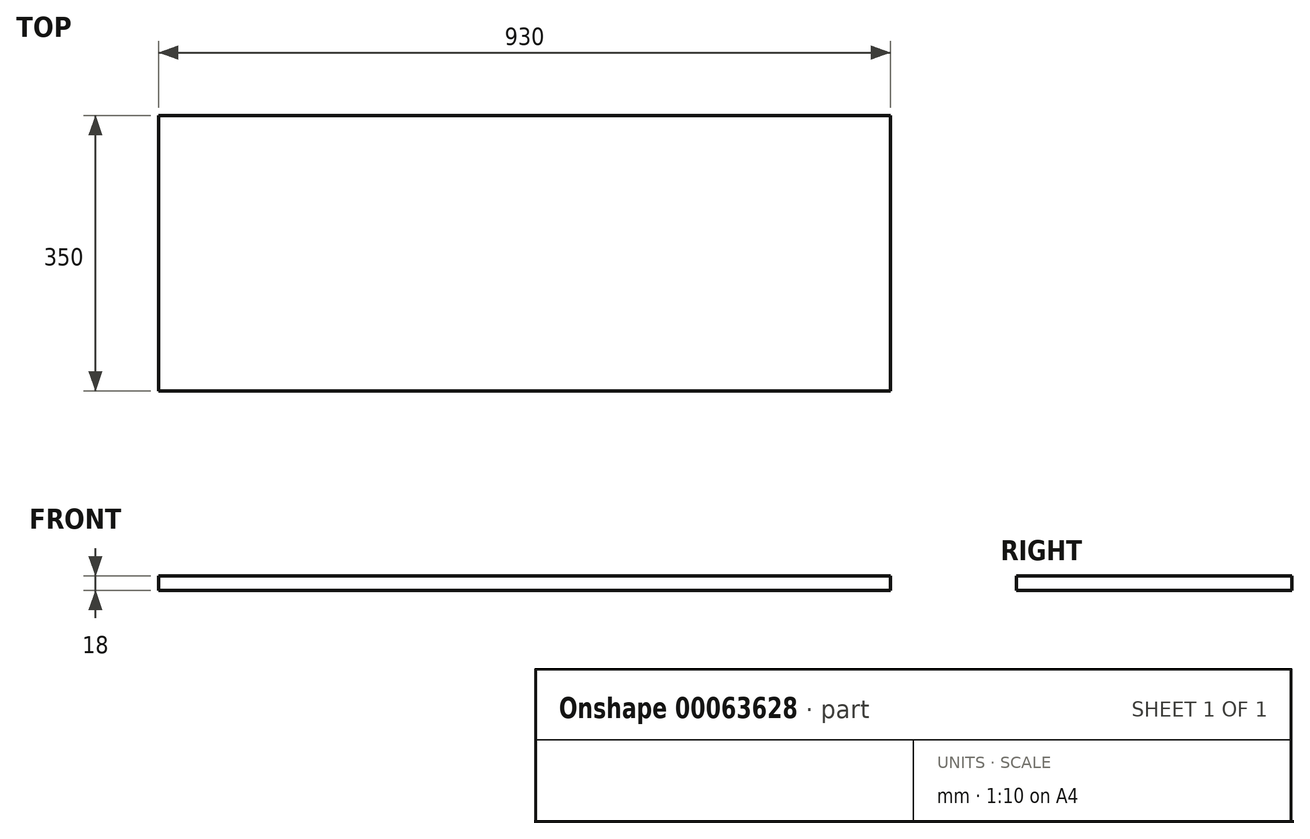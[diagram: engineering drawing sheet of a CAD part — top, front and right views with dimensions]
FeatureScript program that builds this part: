
annotation { "Feature Type Name" : "Feature", "Feature Type Description" : "" }
export const myFeature = defineFeature(function(context is Context, id is Id, definition is map)
    precondition{}
    {
        {
            var Q0;
            Q0=qCreatedBy(makeId("Top.planeOp"),FACE);
            var sketch = newSketch(context, id + "F0", { "sketchPlane" : qUnion([Q0])});
            skLineSegment(sketch, "E0.bottom", {"start": v(0, 0) * mm, "end": v(930, 0) * mm});
            skLineSegment(sketch, "E0.top", {"start": v(0, -350) * mm, "end": v(930, -350) * mm});
            skLineSegment(sketch, "E0.left", {"start": v(0, 0) * mm, "end": v(0, -350) * mm});
            skLineSegment(sketch, "E0.right", {"start": v(930, 0) * mm, "end": v(930, -350) * mm});
            skSolve(sketch);
        }
        {
            var Q0;
            Q0=makeQuery(id+"F0.imprint","IMPRINT",FACE,{"disambiguationData":[TD([[makeQuery(id+"F0.imprint","IMPRINT",EDGE,{"derivedFrom":sQuery(id+"F0.wireOp",EDGE,"E0.bottom")}),-1.0]])]});
            extrude(context, id + "F1", {"entities" : qUnion([Q0]), "depth" : 18 * mm});
        }
    });
